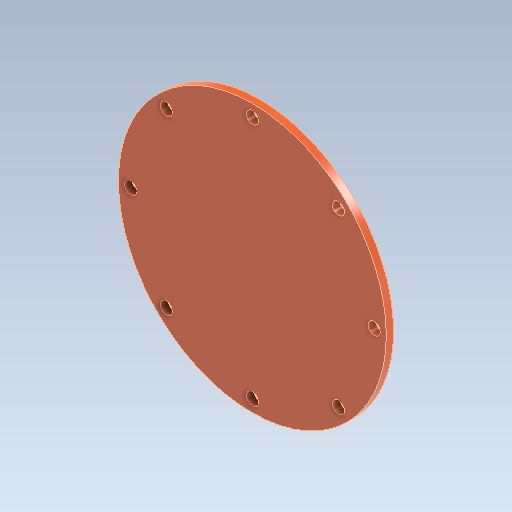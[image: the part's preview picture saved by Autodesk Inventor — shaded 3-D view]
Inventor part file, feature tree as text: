
AUTODESK INVENTOR PART (.ipt)
format: ipt  version: 2021 (Build 250183000, 183)  size: 112,640 bytes
history: native  units: mm
features: sketch x2, other x1, extrude x1, hole x1
ambient origin geometry x8: Origin, YZ Plane, XZ Plane, XY Plane, X Axis, Y Axis, Z Axis, Center Point
bodies: Body1 (feature_tree)
feature tree (5):
  other  "Sólido1"
  extrude  "Extrusión1"  Depth=3.0mm TaperAngle=360.0deg
  hole  "Agujero1"  [1 undecoded]
  sketch  "Boceto1"  dims[d1=3.0mm d2=0.0mm d5=80.0mm d7=360.0deg]
  sketch  "Boceto2"  dims[d9=5.0mm d10=6.0mm d11=4.0mm d12=2.0mm d13=90.0deg d14=8.0mm d15=20.594885mm]
note: 1 required parameter value undecoded (feature->parameter linkage not recoverable at this tier; creation-order binding heuristic only, values carry confidence <= 0.55)
